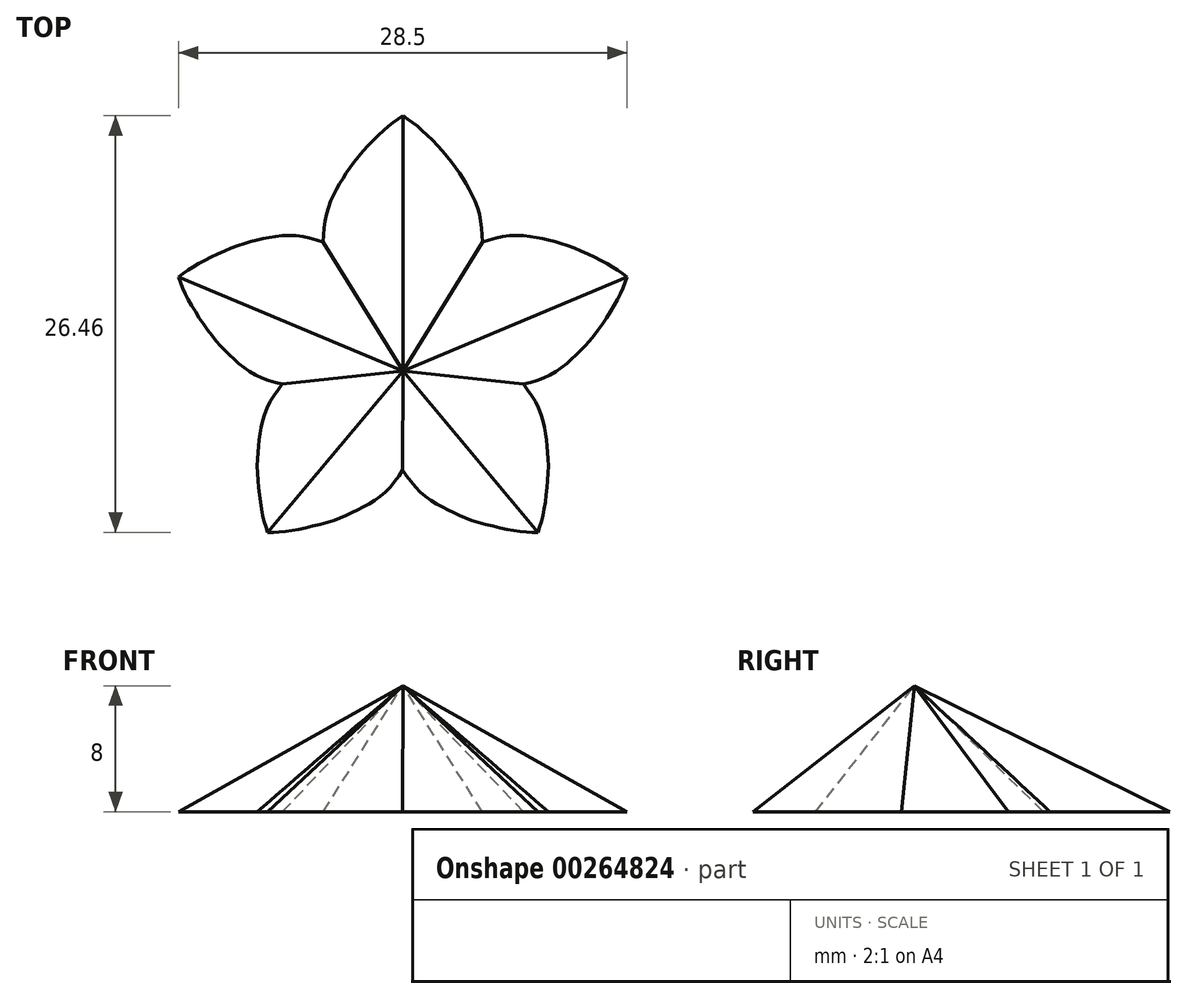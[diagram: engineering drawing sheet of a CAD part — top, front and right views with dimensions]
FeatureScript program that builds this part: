
annotation { "Feature Type Name" : "Feature", "Feature Type Description" : "" }
export const myFeature = defineFeature(function(context is Context, id is Id, definition is map)
    precondition{}
    {
        {
            var Q0;
            Q0=qCreatedBy(makeId("Top.planeOp"),FACE);
            var sketch = newSketch(context, id + "F0", { "sketchPlane" : qUnion([Q0])});
            skFitSpline(sketch, "E0", {"points": [v(0, -3.37) * mm, v(0.92, -4.59) * mm, v(2.08, -5.5) * mm, v(3.19, -6.07) * mm, v(4.43, -6.6) * mm, v(6.05, -7.03) * mm, v(7.5, -7.29) * mm, v(8.58, -7.34) * mm], "startDerivative": vector(5.74, -8.59) * mm, "endDerivative": vector(8.37, -0.22) * mm});
            skFitSpline(sketch, "E1.MirrorCS", {"points": [v(0, -3.37) * mm, v(-0.92, -4.59) * mm, v(-2.08, -5.5) * mm, v(-3.19, -6.07) * mm, v(-4.43, -6.6) * mm, v(-6.05, -7.03) * mm, v(-7.5, -7.29) * mm, v(-8.58, -7.34) * mm], "startDerivative": vector(-5.74, -8.59) * mm, "endDerivative": vector(-8.37, -0.22) * mm});
            skFitSpline(sketch, "E2.MirrorCS", {"points": [v(-7.66, 2.07) * mm, v(-8.5, 0.8) * mm, v(-8.99, -0.6) * mm, v(-9.16, -1.83) * mm, v(-9.24, -3.18) * mm, v(-9.12, -4.85) * mm, v(-8.9, -6.3) * mm, v(-8.58, -7.34) * mm], "startDerivative": vector(-6.22, -8.25) * mm, "endDerivative": vector(2.55, -7.97) * mm});
            skFitSpline(sketch, "E3.MirrorCS", {"points": [v(7.66, 2.07) * mm, v(8.5, 0.8) * mm, v(8.99, -0.6) * mm, v(9.16, -1.83) * mm, v(9.24, -3.18) * mm, v(9.12, -4.85) * mm, v(8.9, -6.3) * mm, v(8.58, -7.34) * mm], "startDerivative": vector(6.22, -8.25) * mm, "endDerivative": vector(-2.55, -7.97) * mm});
            skFitSpline(sketch, "E4.MirrorCS", {"points": [v(-7.66, 2.07) * mm, v(-9.12, 2.54) * mm, v(-10.36, 3.34) * mm, v(-11.27, 4.19) * mm, v(-12.16, 5.2) * mm, v(-13.11, 6.58) * mm, v(-13.83, 7.85) * mm, v(-14.25, 8.86) * mm], "startDerivative": vector(-10, 2.59) * mm, "endDerivative": vector(-2.97, 7.83) * mm});
            skFitSpline(sketch, "E5.MirrorCS", {"points": [v(-5.05, 11.1) * mm, v(-6.53, 11.48) * mm, v(-8.01, 11.47) * mm, v(-9.23, 11.23) * mm, v(-10.53, 10.86) * mm, v(-12.07, 10.2) * mm, v(-13.35, 9.5) * mm, v(-14.25, 8.86) * mm], "startDerivative": vector(-9.84, 3.15) * mm, "endDerivative": vector(-6.68, -5.04) * mm});
            skFitSpline(sketch, "E6.MirrorCS", {"points": [v(7.66, 2.07) * mm, v(9.12, 2.54) * mm, v(10.36, 3.34) * mm, v(11.27, 4.19) * mm, v(12.16, 5.2) * mm, v(13.11, 6.58) * mm, v(13.83, 7.85) * mm, v(14.25, 8.86) * mm], "startDerivative": vector(10, 2.59) * mm, "endDerivative": vector(2.97, 7.83) * mm});
            skFitSpline(sketch, "E7.MirrorCS", {"points": [v(-5.05, 11.1) * mm, v(-4.91, 12.63) * mm, v(-4.44, 14.03) * mm, v(-3.83, 15.12) * mm, v(-3.07, 16.23) * mm, v(-1.95, 17.48) * mm, v(-0.89, 18.48) * mm, v(0.01, 19.13) * mm], "startDerivative": vector(0.1, 10.33) * mm, "endDerivative": vector(6.89, 4.76) * mm});
            skFitSpline(sketch, "E8.MirrorCS", {"points": [v(5.05, 11.1) * mm, v(6.53, 11.48) * mm, v(8.01, 11.47) * mm, v(9.23, 11.23) * mm, v(10.53, 10.86) * mm, v(12.07, 10.2) * mm, v(13.35, 9.5) * mm, v(14.25, 8.86) * mm], "startDerivative": vector(9.84, 3.15) * mm, "endDerivative": vector(6.68, -5.04) * mm});
            skFitSpline(sketch, "E9.MirrorCS", {"points": [v(5.05, 11.1) * mm, v(4.91, 12.63) * mm, v(4.44, 14.03) * mm, v(3.83, 15.12) * mm, v(3.07, 16.23) * mm, v(1.95, 17.48) * mm, v(0.89, 18.48) * mm, v(0, 19.13) * mm], "startDerivative": vector(-0.1, 10.33) * mm, "endDerivative": vector(-6.89, 4.76) * mm});
            skLineSegment(sketch, "E10", {"start": v(0.01, 19.13) * mm, "end": v(0, -3.37) * mm, "construction": true});
            skPoint(sketch, "E11.0.midPoint", {"position": v(0, 10.36) * mm});
            skSolve(sketch);
        }
        {
            var Q0;
            Q0=qCreatedBy(makeId("Top.planeOp"),FACE);
            cPlane(context, id + "F1", {"entities" : qUnion([Q0]), "cplaneType" : CPlaneType.OFFSET, "offset" : 8 * mm, "width" : 150 * mm, "height" : 150 * mm});
        }
        {
            var Q0;
            Q0=qCreatedBy(id+"F1.planeOp",FACE);
            var sketch = newSketch(context, id + "F2", { "sketchPlane" : qUnion([Q0])});
            skPoint(sketch, "E12", {"position": v(0, 2.92) * mm});
            skSolve(sketch);
        }
        {
            var Q0;
            {var subQ1=sQuery(id+"F0.wireOp",EDGE,"E2.MirrorCS");Q0=makeQuery(id+"F0.imprint","IMPRINT",FACE,{"disambiguationData":[TD([[makeQuery(id+"F0.imprint","IMPRINT",EDGE,{"derivedFrom":subQ1}),1.0]])]});}
            var Q1;
            Q1=sQuery(id+"F2.wireOp",VERTEX,"E12");
            loft(context, id + "F3", {"sheetProfilesArray" : [{ "sheetProfileEntities" : qUnion([Q0]) }, { "sheetProfileEntities" : qUnion([Q1]) }]});
        }
    });
